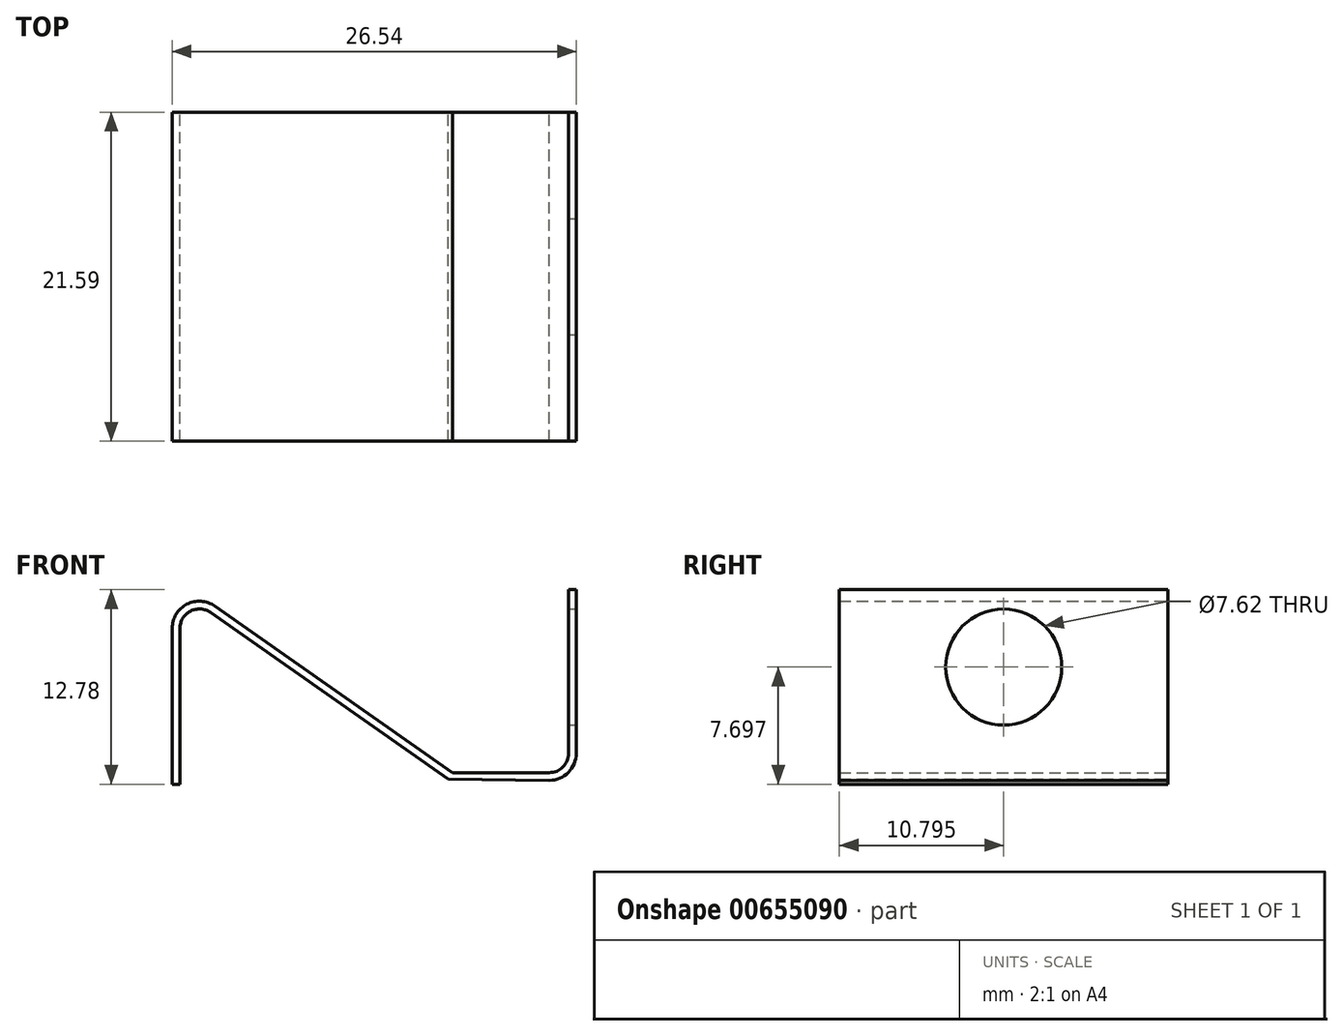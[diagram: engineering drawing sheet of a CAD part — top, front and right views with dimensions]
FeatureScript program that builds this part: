
annotation { "Feature Type Name" : "Feature", "Feature Type Description" : "" }
export const myFeature = defineFeature(function(context is Context, id is Id, definition is map)
    precondition{}
    {
        {
            var Q0;
            Q0=qCreatedBy(makeId("Front.planeOp"),FACE);
            var sketch = newSketch(context, id + "F0", { "sketchPlane" : qUnion([Q0])});
            skLineSegment(sketch, "E0.bottom", {"start": v(-16.05, -0.23) * mm, "end": v(-16.56, -0.23) * mm});
            skLineSegment(sketch, "E0.left", {"start": v(-16.05, -0.23) * mm, "end": v(-16.05, 10.01) * mm});
            skLineSegment(sketch, "E0.right", {"start": v(-16.56, -0.23) * mm, "end": v(-16.56, 10.01) * mm});
            skLineSegment(sketch, "E1", {"start": v(-13.76, 11.47) * mm, "end": v(1.85, 0.53) * mm});
            skLineSegment(sketch, "E2", {"start": v(9.47, 12.55) * mm, "end": v(9.98, 12.55) * mm});
            skLineSegment(sketch, "E3", {"start": v(1.56, 0.12) * mm, "end": v(-14.05, 11.05) * mm});
            skPoint(sketch, "E4.visualSharp", {"position": v(-16.05, 12.45) * mm});
            skArc(sketch, "E4.filletArc", {"start": v(-14.05, 11.05) * mm, "mid": v(-15.37, 11.14) * mm, "end": v(-16.05, 10.01) * mm});
            skArc(sketch, "E5.0", {"start": v(-13.76, 11.47) * mm, "mid": v(-15.6, 11.59) * mm, "end": v(-16.56, 10.01) * mm});
            skPoint(sketch, "E6.visualSharp", {"position": v(13.27, -7.46) * mm});
            skLineSegment(sketch, "E7", {"start": v(1.85, 0.53) * mm, "end": v(8.2, 0.53) * mm});
            skPoint(sketch, "E8.visualSharp", {"position": v(13.92, 0.53) * mm});
            skArc(sketch, "E8.filletArc", {"start": v(8.2, 0.53) * mm, "mid": v(9.1, 0.9) * mm, "end": v(9.47, 1.8) * mm});
            skArc(sketch, "E9.0", {"start": v(8.2, 0.03) * mm, "mid": v(9.46, 0.55) * mm, "end": v(9.98, 1.8) * mm});
            skLineSegment(sketch, "E10", {"start": v(9.47, 12.55) * mm, "end": v(9.47, 1.8) * mm});
            skLineSegment(sketch, "E11", {"start": v(9.98, 12.55) * mm, "end": v(9.98, 1.8) * mm});
            skLineSegment(sketch, "E12", {"start": v(8.2, 0.03) * mm, "end": v(1.56, 0.12) * mm});
            skSolve(sketch);
        }
        {
            var Q0;
            Q0 = qSketchRegion(id + "F0", true);
            extrude(context, id + "F1", {"entities" : qUnion([Q0]), "depth" : 21.59 * mm, "offsetDistance" : 25.4 * mm});
        }
        {
            var Q0;
            Q0=makeQuery(id+"F1.opExtrude","SWEPT_FACE",FACE,{"disambiguationData":[OSD([sQuery(id+"F0.wireOp",EDGE,"E11")])]});
            var sketch = newSketch(context, id + "F2", { "sketchPlane" : qUnion([Q0])});
            skCircle(sketch, "E13", {"center": v(-10.8, 7.47) * mm, "radius": 3.81 * mm});
            skSolve(sketch);
        }
        {
            var Q0;
            Q0 = qSketchRegion(id + "F2", true);
            var Q1;
            Q1=makeQuery(id+"F1.opExtrude","SWEPT_FACE",FACE,{"disambiguationData":[OSD([sQuery(id+"F0.wireOp",EDGE,"E10")])]});
            extrude(context, id + "F3", {"entities" : qUnion([Q0]), "operationType" : NewBodyOperationType.REMOVE, "endBound" : BoundingType.UP_TO_SURFACE, "oppositeDirection" : true, "depth" : 25.4 * mm, "endBoundEntityFace" : qUnion([Q1]), "offsetDistance" : 25.4 * mm});
        }
    });
